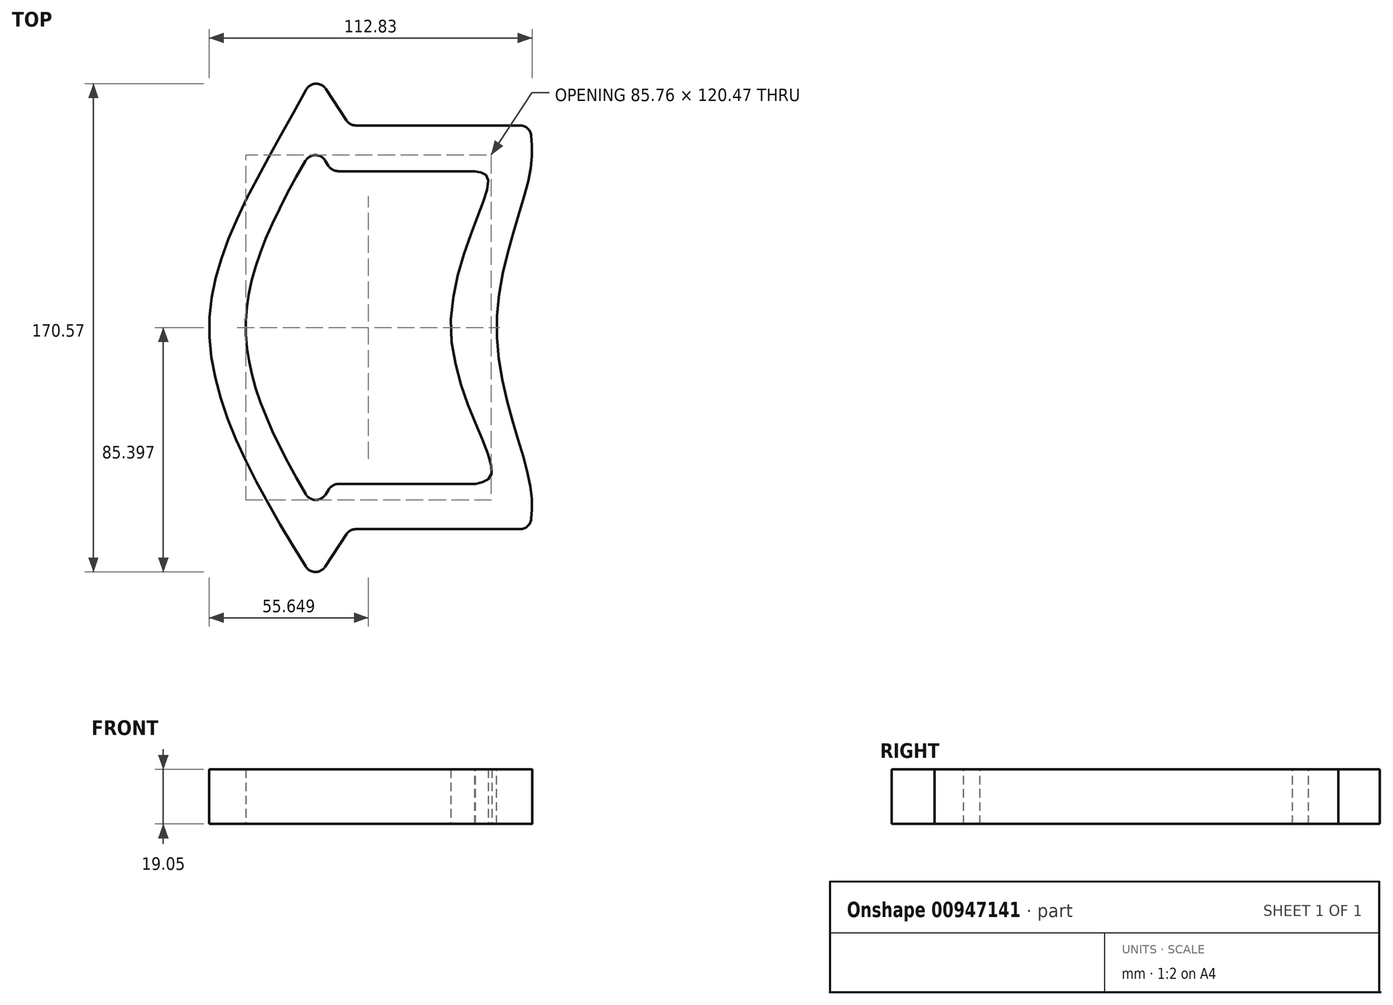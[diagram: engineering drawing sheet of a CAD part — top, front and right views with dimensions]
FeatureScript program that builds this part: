
annotation { "Feature Type Name" : "Feature", "Feature Type Description" : "" }
export const myFeature = defineFeature(function(context is Context, id is Id, definition is map)
    precondition{}
    {
        {
            var Q0;
            Q0=qCreatedBy(makeId("Top.planeOp"),FACE);
            var sketch = newSketch(context, id + "F0", { "sketchPlane" : qUnion([Q0])});
            skFitSpline(sketch, "E0", {"points": [v(0, -88.9) * mm, v(-37.02, 0) * mm, v(0, 88.9) * mm], "startDerivative": vector(-112.57, 180.16) * mm, "endDerivative": vector(109.83, 208) * mm});
            skLineSegment(sketch, "E1", {"start": v(0, 88.9) * mm, "end": v(12.1, 70.52) * mm});
            skLineSegment(sketch, "E2", {"start": v(12.1, 70.52) * mm, "end": v(75.1, 70.52) * mm});
            skLineSegment(sketch, "E3", {"start": v(0, -88.9) * mm, "end": v(12.1, -70.52) * mm});
            skLineSegment(sketch, "E4", {"start": v(12.1, -70.52) * mm, "end": v(75.1, -70.52) * mm});
            skFitSpline(sketch, "E5", {"points": [v(75.1, 70.52) * mm, v(75.1, 54.14) * mm, v(63.4, 0) * mm, v(75.1, -54.79) * mm, v(75.1, -70.52) * mm], "startDerivative": vector(9.33, -79.6) * mm, "endDerivative": vector(-9.17, -77.25) * mm});
            skSolve(sketch);
        }
        {
            var Q0;
            Q0 = qSketchRegion(id + "F0", true);
            extrude(context, id + "F1", {"entities" : qUnion([Q0]), "depth" : 19.05 * mm, "offsetDistance" : 25 * mm});
        }
        {
            var Q0;
            Q0=makeQuery(id+"F1.opExtrude","CAP_FACE",FACE,{"disambiguationData":[OSD([sQuery(id+"F0.wireOp",EDGE,"E0"),sQuery(id+"F0.wireOp",EDGE,"E1"),sQuery(id+"F0.wireOp",EDGE,"E2"),sQuery(id+"F0.wireOp",EDGE,"E3"),sQuery(id+"F0.wireOp",EDGE,"E4"),sQuery(id+"F0.wireOp",EDGE,"E5")])],"isStart":false});
            var sketch = newSketch(context, id + "F2", { "sketchPlane" : qUnion([Q0])});
            skLineSegment(sketch, "E6", {"start": v(0, -63.9) * mm, "end": v(6.05, -54.71) * mm});
            skPoint(sketch, "E6.endSnap0", {"position": v(6.05, -79.71) * mm});
            skLineSegment(sketch, "E7", {"start": v(6.05, -54.71) * mm, "end": v(56.05, -54.71) * mm});
            skFitSpline(sketch, "E8", {"points": [v(0, -63.9) * mm, v(-24.25, 0) * mm, v(0, 63.9) * mm], "startDerivative": vector(-90.04, 152.03) * mm, "endDerivative": vector(90.12, 151.26) * mm});
            skLineSegment(sketch, "E9", {"start": v(0, 63.9) * mm, "end": v(5.78, 54.54) * mm});
            skLineSegment(sketch, "E10", {"start": v(5.78, 54.54) * mm, "end": v(55.78, 54.54) * mm});
            skFitSpline(sketch, "E11", {"points": [v(55.78, 54.54) * mm, v(60.37, 52.05) * mm, v(47.4, 0) * mm, v(61.6, -51.1) * mm, v(56.05, -54.71) * mm], "startDerivative": vector(52.57, -7.14) * mm, "endDerivative": vector(-57.67, -13.25) * mm});
            skSolve(sketch);
        }
        {
            var Q0;
            Q0=makeQuery(id+"F2.imprint","IMPRINT",FACE,{"disambiguationData":[TD([[makeQuery(id+"F2.imprint","IMPRINT",EDGE,{"derivedFrom":sQuery(id+"F2.wireOp",EDGE,"E6")}),1.0]])]});
            extrude(context, id + "F3", {"entities" : qUnion([Q0]), "operationType" : NewBodyOperationType.REMOVE, "oppositeDirection" : true, "depth" : 19.05 * mm, "offsetDistance" : 25 * mm});
        }
        {
            var Q0;
            Q0=makeQuery(id+"F1.opExtrude","SWEPT_EDGE",EDGE,{"disambiguationData":[OSD([sQuery(id+"F0.wireOp",EDGE,"E0"),sQuery(id+"F0.wireOp",EDGE,"E3")])]});
            var Q1;
            Q1=makeQuery(id+"F1.opExtrude","SWEPT_EDGE",EDGE,{"disambiguationData":[OSD([sQuery(id+"F0.wireOp",EDGE,"E4"),sQuery(id+"F0.wireOp",EDGE,"E5")])]});
            var Q2;
            Q2=makeQuery(id+"F3.boolean.opBoolean","COPY",EDGE,{"derivedFrom":makeQuery(id+"F3.opExtrude","SWEPT_EDGE",EDGE,{"disambiguationData":[OSD([sQuery(id+"F2.wireOp",EDGE,"E9"),sQuery(id+"F2.wireOp",EDGE,"E10")])]})});
            var Q3;
            Q3=makeQuery(id+"F1.opExtrude","SWEPT_EDGE",EDGE,{"disambiguationData":[OSD([sQuery(id+"F0.wireOp",EDGE,"E2"),sQuery(id+"F0.wireOp",EDGE,"E5")])]});
            var Q4;
            Q4=makeQuery(id+"F1.opExtrude","SWEPT_EDGE",EDGE,{"disambiguationData":[OSD([sQuery(id+"F0.wireOp",EDGE,"E0"),sQuery(id+"F0.wireOp",EDGE,"E1")])]});
            var Q5;
            Q5=makeQuery(id+"F1.opExtrude","SWEPT_EDGE",EDGE,{"disambiguationData":[OSD([sQuery(id+"F0.wireOp",EDGE,"E1"),sQuery(id+"F0.wireOp",EDGE,"E2")])]});
            var Q6;
            Q6=makeQuery(id+"F1.opExtrude","SWEPT_EDGE",EDGE,{"disambiguationData":[OSD([sQuery(id+"F0.wireOp",EDGE,"E3"),sQuery(id+"F0.wireOp",EDGE,"E4")])]});
            var Q7;
            Q7=makeQuery(id+"F3.boolean.opBoolean","COPY",EDGE,{"derivedFrom":makeQuery(id+"F3.opExtrude","SWEPT_EDGE",EDGE,{"disambiguationData":[OSD([sQuery(id+"F2.wireOp",EDGE,"E8"),sQuery(id+"F2.wireOp",EDGE,"E9")])]})});
            var Q8;
            Q8=makeQuery(id+"F3.boolean.opBoolean","COPY",EDGE,{"derivedFrom":makeQuery(id+"F3.opExtrude","SWEPT_EDGE",EDGE,{"disambiguationData":[OSD([sQuery(id+"F2.wireOp",EDGE,"E6"),sQuery(id+"F2.wireOp",EDGE,"E8")])]})});
            var Q9;
            Q9=makeQuery(id+"F3.boolean.opBoolean","COPY",EDGE,{"derivedFrom":makeQuery(id+"F3.opExtrude","SWEPT_EDGE",EDGE,{"disambiguationData":[OSD([sQuery(id+"F2.wireOp",EDGE,"E6"),sQuery(id+"F2.wireOp",EDGE,"E7")])]})});
            fillet(context, id + "F4", {"entities" : qUnion([Q0, Q1, Q2, Q3, Q4, Q5, Q6, Q7, Q8, Q9]), "radius" : 4 * mm, "tangentPropagation" : true, "allowEdgeOverflow" : false});
        }
    });
